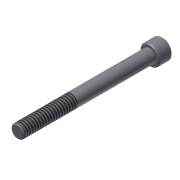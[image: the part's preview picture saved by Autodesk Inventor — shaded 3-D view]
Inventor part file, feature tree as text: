
AUTODESK INVENTOR PART (.ipt)
format: ipt  version: 2011 (Build 150239000, 239)  size: 99,328 bytes
history: native  units: in
note: dims shown in document units (in); Inventor stores cm internally (conversion verified against a paired STEP export)
features: extrude x3, sketch x3, chamfer x1, thread x1
ambient origin geometry x8: Origin, YZ Plane, XZ Plane, XY Plane, X Axis, Y Axis, Z Axis, Center Point
bodies: Solid1 (feature_tree)
feature tree (8):
  extrude  "Extrusion1"  Depth=2.5in TaperAngle=0.0deg
  extrude  "Extrusion2"  Depth=0.25in TaperAngle=0.0deg
  extrude  "Extrusion3"  Depth=0.125in TaperAngle=0.0deg
  chamfer  "Chamfer1"  Distance=0.02in Angle=45.0deg
  thread  "Thread1"  [1 undecoded]
  sketch  "Sketch1"  dims[d0=0.25in d1=2.5in d2=0.0in]
  sketch  "Sketch2"  dims[d3=0.375in d4=0.25in d5=0.0in]
  sketch  "Sketch3"  dims[d6=0.1875in d7=0.125in d8=0.0in d9=0.02in d10=0.125in d11=45.0deg d12=1.0in d13=0.0in]
note: 1 required parameter value undecoded (feature->parameter linkage not recoverable at this tier; creation-order binding heuristic only, values carry confidence <= 0.55)
